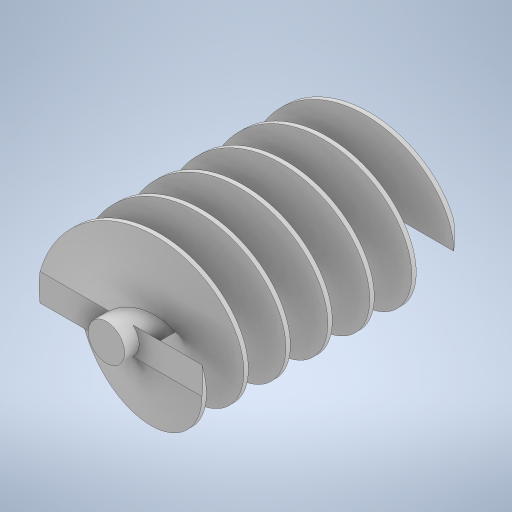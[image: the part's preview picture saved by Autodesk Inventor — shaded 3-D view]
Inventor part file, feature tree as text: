
AUTODESK INVENTOR PART (.ipt)
format: ipt  version: 2023 (Build 270158000, 158)  size: 1,448,960 bytes
history: native  units: in
note: dims shown in document units (in); Inventor stores cm internally (conversion verified against a paired STEP export)
features: extrude x4, sketch x3, other x2, sweep x1
ambient origin geometry x8: Origin, YZ Plane, XZ Plane, XY Plane, X Axis, Y Axis, Z Axis, Center Point
bodies: Solid1 (feature_tree)
feature tree (10):
  sketch  "Sketch1"  dims[d0=1.7717in d1=0.3937in]
  extrude  "Extrusion1"  Depth=0.3937in
  sketch  "Sketch2"  dims[d2=2.7165in d3=0.0in d4=2.7165in d5=1.1811in d6=0.5906in d7=0.0in d10=0.0in d11=0.0in d12=0.0984in d13=0.0984in d14=0.5906in d15=0.0in d18=0.1575in d19=0.0in d20=0.3543in d21=0.0in]
  other  "Work Axis1"
  sketch  "3D Sketch1"
  sweep  "Sweep1"
  extrude  "Extrusion3"  TaperAngle=0.0deg  [1 undecoded]
  extrude  "Extrusion4"  Depth=0.3543in
  extrude  "Extrusion5"  Depth=0.3543in
  other  "Helical Curve1"
note: 1 required parameter value undecoded (feature->parameter linkage not recoverable at this tier; creation-order binding heuristic only, values carry confidence <= 0.55)
